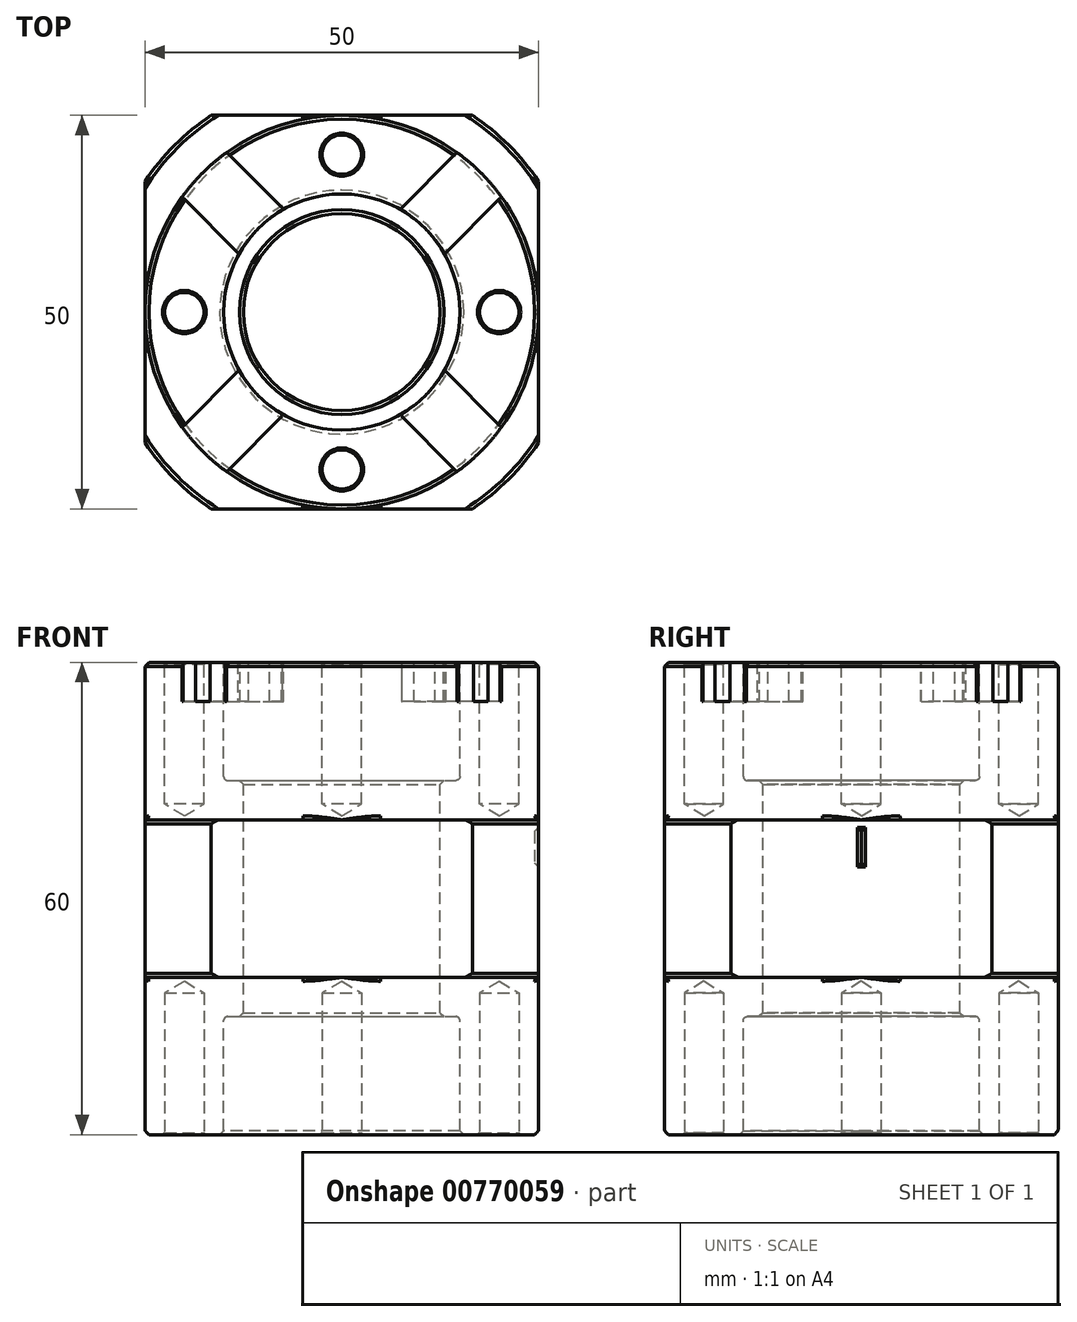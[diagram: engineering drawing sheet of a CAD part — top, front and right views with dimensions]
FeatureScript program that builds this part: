
annotation { "Feature Type Name" : "Feature", "Feature Type Description" : "" }
export const myFeature = defineFeature(function(context is Context, id is Id, definition is map)
    precondition{}
    {
        {
            var Q0;
            Q0=qCreatedBy(makeId("Front.planeOp"),FACE);
            var sketch = newSketch(context, id + "F0", { "sketchPlane" : qUnion([Q0])});
            skLineSegment(sketch, "E0", {"start": v(0, 0) * mm, "end": v(0, -30) * mm, "construction": true});
            skLineSegment(sketch, "E1", {"start": v(15, 0) * mm, "end": v(25, 0) * mm});
            skLineSegment(sketch, "E2", {"start": v(25, -20) * mm, "end": v(30, -20) * mm});
            skLineSegment(sketch, "E3", {"start": v(30, -20) * mm, "end": v(30, -30) * mm});
            skLineSegment(sketch, "E4", {"start": v(15, 0) * mm, "end": v(15, -15) * mm});
            skLineSegment(sketch, "E5", {"start": v(15, -15) * mm, "end": v(12.5, -15) * mm});
            skLineSegment(sketch, "E6", {"start": v(12.5, -15) * mm, "end": v(12.5, -30) * mm});
            skLineSegment(sketch, "E7", {"start": v(25, 0) * mm, "end": v(25, -20) * mm});
            skLineSegment(sketch, "E8", {"start": v(12.5, -30) * mm, "end": v(30, -30) * mm, "construction": true});
            skLineSegment(sketch, "E9.MirrorCS", {"start": v(15, -60) * mm, "end": v(25, -60) * mm});
            skLineSegment(sketch, "E10.MirrorCS", {"start": v(15, -45) * mm, "end": v(12.5, -45) * mm});
            skLineSegment(sketch, "E11.MirrorCS", {"start": v(30, -40) * mm, "end": v(30, -30) * mm});
            skLineSegment(sketch, "E12.MirrorCS", {"start": v(12.5, -45) * mm, "end": v(12.5, -30) * mm});
            skLineSegment(sketch, "E13.MirrorCS", {"start": v(25, -60) * mm, "end": v(25, -40) * mm});
            skLineSegment(sketch, "E14.MirrorCS", {"start": v(15, -60) * mm, "end": v(15, -45) * mm});
            skLineSegment(sketch, "E15.MirrorCS", {"start": v(25, -40) * mm, "end": v(30, -40) * mm});
            skSolve(sketch);
        }
        {
            var Q0;
            Q0 = qSketchRegion(id + "F0", true);
            var Q1;
            Q1=sQuery(id+"F0.wireOp",EDGE,"E0");
            revolve(context, id + "F1", {"surfaceOperationType" : NewSurfaceOperationType.NEW, "entities" : qUnion([Q0]), "axis" : qUnion([Q1]), "revolveType" : RevolveType.FULL});
        }
        {
            var Q0;
            Q0=makeQuery(id+"F1.opRevolve","SWEPT_FACE",FACE,{"disambiguationData":[OSD([sQuery(id+"F0.wireOp",EDGE,"E2")])]});
            var sketch = newSketch(context, id + "F2", { "sketchPlane" : qUnion([Q0])});
            skPoint(sketch, "E16.middle", {"position": v(0, 0) * mm});
            skLineSegment(sketch, "E17.bottom", {"start": v(-30, 30) * mm, "end": v(30, 30) * mm});
            skLineSegment(sketch, "E17.top", {"start": v(-30, -30) * mm, "end": v(30, -30) * mm});
            skLineSegment(sketch, "E17.left", {"start": v(-30, 30) * mm, "end": v(-30, -30) * mm});
            skLineSegment(sketch, "E17.right", {"start": v(30, 30) * mm, "end": v(30, -30) * mm});
            skLineSegment(sketch, "E18.bottom", {"start": v(-25, 25) * mm, "end": v(25, 25) * mm});
            skLineSegment(sketch, "E18.top", {"start": v(-25, -25) * mm, "end": v(25, -25) * mm});
            skLineSegment(sketch, "E18.left", {"start": v(-25, 25) * mm, "end": v(-25, -25) * mm});
            skLineSegment(sketch, "E18.right", {"start": v(25, 25) * mm, "end": v(25, -25) * mm});
            skSolve(sketch);
        }
        {
            var Q0;
            {var subQ0=sQuery(id+"F2.wireOp",EDGE,"E18.bottom");var subQ1=sQuery(id+"F0.wireOp",EDGE,"E2");var subQ2=makeQuery(id+"F1.opRevolve","SWEPT_EDGE",EDGE,{"disambiguationData":[OSD([subQ1,sQuery(id+"F0.wireOp",EDGE,"E3")])]});var subQ3=makeQuery(id+"F2.imprint","INTERSECT",VERTEX,{"disambiguationData":[OD(0.0)],"derivedFrom":[subQ2,subQ0]});Q0=makeQuery(id+"F2.imprint","IMPRINT",FACE,{"disambiguationData":[TD([[makeQuery(id+"F2.imprint","IMPRINT",EDGE,{"disambiguationData":[TD([[subQ3,-1.0]])],"derivedFrom":subQ0}),1.0]])]});}
            var Q1;
            {var subQ0=sQuery(id+"F2.wireOp",EDGE,"E18.right");var subQ1=sQuery(id+"F0.wireOp",EDGE,"E2");var subQ2=makeQuery(id+"F1.opRevolve","SWEPT_EDGE",EDGE,{"disambiguationData":[OSD([subQ1,sQuery(id+"F0.wireOp",EDGE,"E3")])]});var subQ3=makeQuery(id+"F2.imprint","INTERSECT",VERTEX,{"disambiguationData":[OD(0.0)],"derivedFrom":[subQ2,subQ0]});Q1=makeQuery(id+"F2.imprint","IMPRINT",FACE,{"disambiguationData":[TD([[makeQuery(id+"F2.imprint","IMPRINT",EDGE,{"disambiguationData":[TD([[subQ3,-1.0]])],"derivedFrom":subQ0}),1.0]])]});}
            var Q2;
            {var subQ0=sQuery(id+"F2.wireOp",EDGE,"E18.left");var subQ1=sQuery(id+"F0.wireOp",EDGE,"E2");var subQ2=makeQuery(id+"F1.opRevolve","SWEPT_EDGE",EDGE,{"disambiguationData":[OSD([subQ1,sQuery(id+"F0.wireOp",EDGE,"E3")])]});var subQ3=makeQuery(id+"F2.imprint","INTERSECT",VERTEX,{"disambiguationData":[OD(0.0)],"derivedFrom":[subQ2,subQ0]});Q2=makeQuery(id+"F2.imprint","IMPRINT",FACE,{"disambiguationData":[TD([[makeQuery(id+"F2.imprint","IMPRINT",EDGE,{"disambiguationData":[TD([[subQ3,-1.0]])],"derivedFrom":subQ0}),-1.0]])]});}
            var Q3;
            {var subQ0=sQuery(id+"F2.wireOp",EDGE,"E18.top");var subQ1=sQuery(id+"F0.wireOp",EDGE,"E2");var subQ2=makeQuery(id+"F1.opRevolve","SWEPT_EDGE",EDGE,{"disambiguationData":[OSD([subQ1,sQuery(id+"F0.wireOp",EDGE,"E3")])]});var subQ3=makeQuery(id+"F2.imprint","INTERSECT",VERTEX,{"disambiguationData":[OD(0.0)],"derivedFrom":[subQ2,subQ0]});Q3=makeQuery(id+"F2.imprint","IMPRINT",FACE,{"disambiguationData":[TD([[makeQuery(id+"F2.imprint","IMPRINT",EDGE,{"disambiguationData":[TD([[subQ3,-1.0]])],"derivedFrom":subQ0}),-1.0]])]});}
            extrude(context, id + "F3", {"entities" : qUnion([Q0, Q1, Q2, Q3]), "operationType" : NewBodyOperationType.REMOVE, "endBound" : BoundingType.UP_TO_NEXT, "oppositeDirection" : true, "depth" : 26 * mm, "offsetDistance" : 25 * mm});
        }
        {
            var Q0;
            Q0=makeQuery(id+"F1.opRevolve","SWEPT_FACE",FACE,{"disambiguationData":[OSD([sQuery(id+"F0.wireOp",EDGE,"E1")])]});
            var sketch = newSketch(context, id + "F4", { "sketchPlane" : qUnion([Q0])});
            skLineSegment(sketch, "E19", {"start": v(0, 0) * mm, "end": v(31.82, 31.82) * mm, "construction": true});
            skPoint(sketch, "E20.center", {"position": v(0, 0) * mm});
            skLineSegment(sketch, "E21", {"start": v(14.62, 20.28) * mm, "end": v(7.4, 13.05) * mm});
            skArc(sketch, "E22", {"start": v(17.68, 17.68) * mm, "mid": v(16.2, 19.04) * mm, "end": v(14.62, 20.28) * mm});
            skArc(sketch, "E23", {"start": v(10.6, 10.6) * mm, "mid": v(9.08, 11.94) * mm, "end": v(7.4, 13.05) * mm});
            skLineSegment(sketch, "E24.MirrorCS", {"start": v(20.28, 14.62) * mm, "end": v(13.05, 7.4) * mm});
            skArc(sketch, "E25.MirrorCS", {"start": v(17.68, 17.68) * mm, "mid": v(19.04, 16.2) * mm, "end": v(20.28, 14.62) * mm});
            skArc(sketch, "E26.MirrorCS", {"start": v(10.6, 10.6) * mm, "mid": v(11.94, 9.08) * mm, "end": v(13.05, 7.4) * mm});
            skLineSegment(sketch, "E27.1.0", {"start": v(-20.28, 14.62) * mm, "end": v(-13.05, 7.4) * mm});
            skArc(sketch, "E27.1.1", {"start": v(-17.68, 17.68) * mm, "mid": v(-19.04, 16.2) * mm, "end": v(-20.28, 14.62) * mm});
            skArc(sketch, "E27.1.2", {"start": v(-17.68, 17.68) * mm, "mid": v(-16.2, 19.04) * mm, "end": v(-14.62, 20.28) * mm});
            skLineSegment(sketch, "E27.1.3", {"start": v(-14.62, 20.28) * mm, "end": v(-7.4, 13.05) * mm});
            skArc(sketch, "E27.1.4", {"start": v(-10.6, 10.6) * mm, "mid": v(-9.08, 11.94) * mm, "end": v(-7.4, 13.05) * mm});
            skArc(sketch, "E27.1.5", {"start": v(-10.6, 10.6) * mm, "mid": v(-11.94, 9.08) * mm, "end": v(-13.05, 7.4) * mm});
            skLineSegment(sketch, "E27.1.6", {"start": v(0, 0) * mm, "end": v(-31.82, 31.82) * mm, "construction": true});
            skLineSegment(sketch, "E27.2.0", {"start": v(-14.62, -20.28) * mm, "end": v(-7.4, -13.05) * mm});
            skArc(sketch, "E27.2.1", {"start": v(-17.68, -17.68) * mm, "mid": v(-16.2, -19.04) * mm, "end": v(-14.62, -20.28) * mm});
            skArc(sketch, "E27.2.2", {"start": v(-17.68, -17.68) * mm, "mid": v(-19.04, -16.2) * mm, "end": v(-20.28, -14.62) * mm});
            skLineSegment(sketch, "E27.2.3", {"start": v(-20.28, -14.62) * mm, "end": v(-13.05, -7.4) * mm});
            skArc(sketch, "E27.2.4", {"start": v(-10.6, -10.6) * mm, "mid": v(-11.94, -9.08) * mm, "end": v(-13.05, -7.4) * mm});
            skArc(sketch, "E27.2.5", {"start": v(-10.6, -10.6) * mm, "mid": v(-9.08, -11.94) * mm, "end": v(-7.4, -13.05) * mm});
            skLineSegment(sketch, "E27.2.6", {"start": v(0, 0) * mm, "end": v(-31.82, -31.82) * mm, "construction": true});
            skLineSegment(sketch, "E27.3.0", {"start": v(20.28, -14.62) * mm, "end": v(13.05, -7.4) * mm});
            skArc(sketch, "E27.3.1", {"start": v(17.68, -17.68) * mm, "mid": v(19.04, -16.2) * mm, "end": v(20.28, -14.62) * mm});
            skArc(sketch, "E27.3.2", {"start": v(17.68, -17.68) * mm, "mid": v(16.2, -19.04) * mm, "end": v(14.62, -20.28) * mm});
            skLineSegment(sketch, "E27.3.3", {"start": v(14.62, -20.28) * mm, "end": v(7.4, -13.05) * mm});
            skArc(sketch, "E27.3.4", {"start": v(10.6, -10.6) * mm, "mid": v(9.08, -11.94) * mm, "end": v(7.4, -13.05) * mm});
            skArc(sketch, "E27.3.5", {"start": v(10.6, -10.6) * mm, "mid": v(11.94, -9.08) * mm, "end": v(13.05, -7.4) * mm});
            skLineSegment(sketch, "E27.3.6", {"start": v(0, 0) * mm, "end": v(31.82, -31.82) * mm, "construction": true});
            skSolve(sketch);
        }
        {
            var Q0;
            Q0 = qSketchRegion(id + "F4", true);
            extrude(context, id + "F5", {"entities" : qUnion([Q0]), "operationType" : NewBodyOperationType.REMOVE, "oppositeDirection" : true, "depth" : 5 * mm, "offsetDistance" : 25 * mm});
        }
        {
            var Q0;
            Q0=makeQuery(id+"F5.boolean.opBoolean","SPLIT",FACE,{"disambiguationData":[TD([makeQuery(id+"F5.opExtrude","SWEPT_FACE",FACE,{"disambiguationData":[OSD([sQuery(id+"F4.wireOp",EDGE,"E21")])]})])],"derivedFrom":makeQuery(id+"F1.opRevolve","SWEPT_FACE",FACE,{"disambiguationData":[OSD([sQuery(id+"F0.wireOp",EDGE,"E1")])]})});
            var sketch = newSketch(context, id + "F6", { "sketchPlane" : qUnion([Q0])});
            skLineSegment(sketch, "E28", {"start": v(0, 0) * mm, "end": v(20, 0) * mm, "construction": true});
            skCircle(sketch, "E29", {"center": v(0, 0) * mm, "radius": 20 * mm, "construction": true});
            skLineSegment(sketch, "E30.1.0", {"start": v(0, 0) * mm, "end": v(0, 20) * mm, "construction": true});
            skLineSegment(sketch, "E30.2.0", {"start": v(0, 0) * mm, "end": v(-20, 0) * mm, "construction": true});
            skLineSegment(sketch, "E30.3.0", {"start": v(0, 0) * mm, "end": v(0, -20) * mm, "construction": true});
            skSolve(sketch);
        }
        {
            var Q0;
            Q0=sQuery(id+"F6.wireOp",VERTEX,"E30.1.0.end");
            var Q1;
            Q1=sQuery(id+"F6.wireOp",VERTEX,"E28.end");
            var Q2;
            Q2=sQuery(id+"F6.wireOp",VERTEX,"E30.3.0.end");
            var Q3;
            Q3=sQuery(id+"F6.wireOp",VERTEX,"E30.2.0.end");
            var Q4;
            Q4=makeQuery(id+"F1.opRevolve","SWEPT_BODY",BODY,{"disambiguationData":[OSD([sQuery(id+"F0.wireOp",EDGE,"E1"),sQuery(id+"F0.wireOp",EDGE,"E2"),sQuery(id+"F0.wireOp",EDGE,"E3"),sQuery(id+"F0.wireOp",EDGE,"E4"),sQuery(id+"F0.wireOp",EDGE,"E5"),sQuery(id+"F0.wireOp",EDGE,"E6"),sQuery(id+"F0.wireOp",EDGE,"E7"),sQuery(id+"F0.wireOp",EDGE,"E9.MirrorCS"),sQuery(id+"F0.wireOp",EDGE,"E10.MirrorCS"),sQuery(id+"F0.wireOp",EDGE,"E11.MirrorCS"),sQuery(id+"F0.wireOp",EDGE,"E12.MirrorCS"),sQuery(id+"F0.wireOp",EDGE,"E13.MirrorCS"),sQuery(id+"F0.wireOp",EDGE,"E14.MirrorCS"),sQuery(id+"F0.wireOp",EDGE,"E15.MirrorCS")])]});
            hole(context, id + "F7", {"style" : HoleStyle.C_SINK, "endStyle" : HoleEndStyle.BLIND, "holeDiameter" : 5 * mm, "cSinkDiameter" : 5.5 * mm, "cSinkAngle" : 90 * degree, "majorDiameter" : 5 * mm, "holeDepth" : 18 * mm, "isTappedThrough" : true, "tappedDepth" : 5 * mm, "tapClearance" : 3, "startFromSketch" : true, "locations" : qUnion([Q0, Q1, Q2, Q3]), "scope" : qUnion([Q4])});
        }
        {
            var Q0;
            Q0=makeQuery(id+"F3.boolean.opBoolean","COPY",FACE,{"derivedFrom":makeQuery(id+"F3.opExtrude","SWEPT_FACE",FACE,{"disambiguationData":[OSD([sQuery(id+"F2.wireOp",EDGE,"E18.right")])]})});
            var sketch = newSketch(context, id + "F8", { "sketchPlane" : qUnion([Q0])});
            skLineSegment(sketch, "E31.bottom", {"start": v(0.5, -26) * mm, "end": v(-0.5, -26) * mm});
            skLineSegment(sketch, "E31.left", {"start": v(0.5, -26) * mm, "end": v(0.5, -21) * mm});
            skLineSegment(sketch, "E31.right", {"start": v(-0.5, -26) * mm, "end": v(-0.5, -21) * mm});
            skPoint(sketch, "E31.middle", {"position": v(0, -20) * mm});
            skLineSegment(sketch, "E32", {"start": v(0.5, -21) * mm, "end": v(-0.5, -21) * mm});
            skSolve(sketch);
        }
        {
            var Q0;
            Q0=makeQuery(id+"F8.imprint","IMPRINT",FACE,{"disambiguationData":[TD([[makeQuery(id+"F8.imprint","IMPRINT",EDGE,{"derivedFrom":sQuery(id+"F8.wireOp",EDGE,"E31.bottom")}),-1.0]])]});
            extrude(context, id + "F9", {"entities" : qUnion([Q0]), "operationType" : NewBodyOperationType.REMOVE, "oppositeDirection" : true, "depth" : 0.5 * mm, "offsetDistance" : 25 * mm, "hasDraft" : true, "draftAngle" : 45 * degree, "draftPullDirection" : true});
        }
        {
            var Q0;
            Q0=makeQuery(id+"F1.opRevolve","SWEPT_FACE",FACE,{"disambiguationData":[OSD([sQuery(id+"F0.wireOp",EDGE,"E9.MirrorCS")])]});
            var sketch = newSketch(context, id + "F10", { "sketchPlane" : qUnion([Q0])});
            skLineSegment(sketch, "E33", {"start": v(0, 0) * mm, "end": v(20, 0) * mm, "construction": true});
            skCircle(sketch, "E34", {"center": v(0, 0) * mm, "radius": 20 * mm, "construction": true});
            skLineSegment(sketch, "E35.1.0", {"start": v(0, 0) * mm, "end": v(0, 20) * mm, "construction": true});
            skLineSegment(sketch, "E35.2.0", {"start": v(0, 0) * mm, "end": v(-20, 0) * mm, "construction": true});
            skLineSegment(sketch, "E35.3.0", {"start": v(0, 0) * mm, "end": v(0, -20) * mm, "construction": true});
            skSolve(sketch);
        }
        {
            var Q0;
            Q0=sQuery(id+"F10.wireOp",VERTEX,"E33.end");
            var Q1;
            Q1=sQuery(id+"F10.wireOp",VERTEX,"E35.1.0.end");
            var Q2;
            Q2=sQuery(id+"F10.wireOp",VERTEX,"E35.2.0.end");
            var Q3;
            Q3=sQuery(id+"F10.wireOp",VERTEX,"E35.3.0.end");
            var Q4;
            Q4=makeQuery(id+"F1.opRevolve","SWEPT_BODY",BODY,{"disambiguationData":[OSD([sQuery(id+"F0.wireOp",EDGE,"E1"),sQuery(id+"F0.wireOp",EDGE,"E2"),sQuery(id+"F0.wireOp",EDGE,"E3"),sQuery(id+"F0.wireOp",EDGE,"E4"),sQuery(id+"F0.wireOp",EDGE,"E5"),sQuery(id+"F0.wireOp",EDGE,"E6"),sQuery(id+"F0.wireOp",EDGE,"E7"),sQuery(id+"F0.wireOp",EDGE,"E9.MirrorCS"),sQuery(id+"F0.wireOp",EDGE,"E10.MirrorCS"),sQuery(id+"F0.wireOp",EDGE,"E11.MirrorCS"),sQuery(id+"F0.wireOp",EDGE,"E12.MirrorCS"),sQuery(id+"F0.wireOp",EDGE,"E13.MirrorCS"),sQuery(id+"F0.wireOp",EDGE,"E14.MirrorCS"),sQuery(id+"F0.wireOp",EDGE,"E15.MirrorCS")])]});
            hole(context, id + "F11", {"style" : HoleStyle.C_SINK, "endStyle" : HoleEndStyle.BLIND, "holeDiameter" : 5 * mm, "cSinkDiameter" : 5.5 * mm, "cSinkAngle" : 90 * degree, "majorDiameter" : 5 * mm, "holeDepth" : 18 * mm, "isTappedThrough" : true, "tappedDepth" : 5 * mm, "tapClearance" : 3, "startFromSketch" : true, "locations" : qUnion([Q0, Q1, Q2, Q3]), "scope" : qUnion([Q4])});
        }
        {
            var Q0;
            Q0=makeQuery(id+"F1.opRevolve","SWEPT_FACE",FACE,{"disambiguationData":[OSD([sQuery(id+"F0.wireOp",EDGE,"E9.MirrorCS")])]});
            var sketch = newSketch(context, id + "F12", { "sketchPlane" : qUnion([Q0])});
            skLineSegment(sketch, "E36", {"start": v(0, 0) * mm, "end": v(31.82, 31.82) * mm, "construction": true});
            skPoint(sketch, "E37.center", {"position": v(0, 0) * mm});
            skLineSegment(sketch, "E38", {"start": v(14.62, 20.28) * mm, "end": v(7.4, 13.05) * mm});
            skArc(sketch, "E39", {"start": v(17.68, 17.68) * mm, "mid": v(16.2, 19.04) * mm, "end": v(14.62, 20.28) * mm});
            skArc(sketch, "E40", {"start": v(10.6, 10.6) * mm, "mid": v(9.08, 11.94) * mm, "end": v(7.4, 13.05) * mm});
            skLineSegment(sketch, "E41.MirrorCS", {"start": v(20.28, 14.62) * mm, "end": v(13.05, 7.4) * mm});
            skArc(sketch, "E42.MirrorCS", {"start": v(17.68, 17.68) * mm, "mid": v(19.04, 16.2) * mm, "end": v(20.28, 14.62) * mm});
            skArc(sketch, "E43.MirrorCS", {"start": v(10.6, 10.6) * mm, "mid": v(11.94, 9.08) * mm, "end": v(13.05, 7.4) * mm});
            skLineSegment(sketch, "E44.1.0", {"start": v(-20.28, 14.62) * mm, "end": v(-13.05, 7.4) * mm});
            skArc(sketch, "E44.1.1", {"start": v(-17.68, 17.68) * mm, "mid": v(-19.04, 16.2) * mm, "end": v(-20.28, 14.62) * mm});
            skArc(sketch, "E44.1.2", {"start": v(-17.68, 17.68) * mm, "mid": v(-16.2, 19.04) * mm, "end": v(-14.62, 20.28) * mm});
            skLineSegment(sketch, "E44.1.3", {"start": v(-14.62, 20.28) * mm, "end": v(-7.4, 13.05) * mm});
            skArc(sketch, "E44.1.4", {"start": v(-10.6, 10.6) * mm, "mid": v(-9.08, 11.94) * mm, "end": v(-7.4, 13.05) * mm});
            skArc(sketch, "E44.1.5", {"start": v(-10.6, 10.6) * mm, "mid": v(-11.94, 9.08) * mm, "end": v(-13.05, 7.4) * mm});
            skLineSegment(sketch, "E44.1.6", {"start": v(0, 0) * mm, "end": v(-31.82, 31.82) * mm, "construction": true});
            skLineSegment(sketch, "E44.2.0", {"start": v(-14.62, -20.28) * mm, "end": v(-7.4, -13.05) * mm});
            skArc(sketch, "E44.2.1", {"start": v(-17.68, -17.68) * mm, "mid": v(-16.2, -19.04) * mm, "end": v(-14.62, -20.28) * mm});
            skArc(sketch, "E44.2.2", {"start": v(-17.68, -17.68) * mm, "mid": v(-19.04, -16.2) * mm, "end": v(-20.28, -14.62) * mm});
            skLineSegment(sketch, "E44.2.3", {"start": v(-20.28, -14.62) * mm, "end": v(-13.05, -7.4) * mm});
            skArc(sketch, "E44.2.4", {"start": v(-10.6, -10.6) * mm, "mid": v(-11.94, -9.08) * mm, "end": v(-13.05, -7.4) * mm});
            skArc(sketch, "E44.2.5", {"start": v(-10.6, -10.6) * mm, "mid": v(-9.08, -11.94) * mm, "end": v(-7.4, -13.05) * mm});
            skLineSegment(sketch, "E44.2.6", {"start": v(0, 0) * mm, "end": v(-31.82, -31.82) * mm, "construction": true});
            skLineSegment(sketch, "E44.3.0", {"start": v(20.28, -14.62) * mm, "end": v(13.05, -7.4) * mm});
            skArc(sketch, "E44.3.1", {"start": v(17.68, -17.68) * mm, "mid": v(19.04, -16.2) * mm, "end": v(20.28, -14.62) * mm});
            skArc(sketch, "E44.3.2", {"start": v(17.68, -17.68) * mm, "mid": v(16.2, -19.04) * mm, "end": v(14.62, -20.28) * mm});
            skLineSegment(sketch, "E44.3.3", {"start": v(14.62, -20.28) * mm, "end": v(7.4, -13.05) * mm});
            skArc(sketch, "E44.3.4", {"start": v(10.6, -10.6) * mm, "mid": v(9.08, -11.94) * mm, "end": v(7.4, -13.05) * mm});
            skArc(sketch, "E44.3.5", {"start": v(10.6, -10.6) * mm, "mid": v(11.94, -9.08) * mm, "end": v(13.05, -7.4) * mm});
            skLineSegment(sketch, "E44.3.6", {"start": v(0, 0) * mm, "end": v(31.82, -31.82) * mm, "construction": true});
            skSolve(sketch);
        }
        {
            var Q0;
            Q0=makeQuery(id+"F12.imprint","IMPRINT",FACE,{"disambiguationData":[TD([[makeQuery(id+"F12.imprint","IMPRINT",EDGE,{"derivedFrom":sQuery(id+"F12.wireOp",EDGE,"E44.1.0")}),1.0]])]});
            var Q1;
            Q1=makeQuery(id+"F12.imprint","IMPRINT",FACE,{"disambiguationData":[TD([[makeQuery(id+"F12.imprint","IMPRINT",EDGE,{"derivedFrom":sQuery(id+"F12.wireOp",EDGE,"E38")}),1.0]])]});
            var Q2;
            Q2=makeQuery(id+"F12.imprint","IMPRINT",FACE,{"disambiguationData":[TD([[makeQuery(id+"F12.imprint","IMPRINT",EDGE,{"derivedFrom":sQuery(id+"F12.wireOp",EDGE,"E44.3.0")}),1.0]])]});
            var Q3;
            Q3=makeQuery(id+"F12.imprint","IMPRINT",FACE,{"disambiguationData":[TD([[makeQuery(id+"F12.imprint","IMPRINT",EDGE,{"derivedFrom":sQuery(id+"F12.wireOp",EDGE,"E44.2.0")}),1.0]])]});
            extrude(context, id + "F13", {"entities" : qUnion([Q0, Q1, Q2, Q3]), "operationType" : NewBodyOperationType.REMOVE, "oppositeDirection" : true, "depth" : 5 * mm, "offsetDistance" : 25 * mm});
        }
        {
            var Q0;
            {var subQ0=sQuery(id+"F0.wireOp",EDGE,"E1");var subQ1=sQuery(id+"F0.wireOp",EDGE,"E7");Q0=makeQuery(id+"F5.boolean.opBoolean","SPLIT",EDGE,{"disambiguationData":[TD([makeQuery(id+"F5.opExtrude","SWEPT_FACE",FACE,{"disambiguationData":[OSD([sQuery(id+"F4.wireOp",EDGE,"E27.1.0")])]})])],"derivedFrom":makeQuery(id+"F1.opRevolve","SWEPT_EDGE",EDGE,{"disambiguationData":[OSD([subQ0,subQ1])]})});}
            var Q1;
            {var subQ0=sQuery(id+"F0.wireOp",EDGE,"E1");var subQ1=sQuery(id+"F0.wireOp",EDGE,"E7");Q1=makeQuery(id+"F5.boolean.opBoolean","SPLIT",EDGE,{"disambiguationData":[TD([makeQuery(id+"F5.opExtrude","SWEPT_FACE",FACE,{"disambiguationData":[OSD([sQuery(id+"F4.wireOp",EDGE,"E21")])]})])],"derivedFrom":makeQuery(id+"F1.opRevolve","SWEPT_EDGE",EDGE,{"disambiguationData":[OSD([subQ0,subQ1])]})});}
            var Q2;
            {var subQ0=sQuery(id+"F0.wireOp",EDGE,"E1");var subQ1=sQuery(id+"F0.wireOp",EDGE,"E7");Q2=makeQuery(id+"F5.boolean.opBoolean","SPLIT",EDGE,{"disambiguationData":[TD([makeQuery(id+"F5.opExtrude","SWEPT_FACE",FACE,{"disambiguationData":[OSD([sQuery(id+"F4.wireOp",EDGE,"E24.MirrorCS")])]})])],"derivedFrom":makeQuery(id+"F1.opRevolve","SWEPT_EDGE",EDGE,{"disambiguationData":[OSD([subQ0,subQ1])]})});}
            var Q3;
            {var subQ0=sQuery(id+"F0.wireOp",EDGE,"E1");var subQ1=sQuery(id+"F0.wireOp",EDGE,"E7");Q3=makeQuery(id+"F5.boolean.opBoolean","SPLIT",EDGE,{"disambiguationData":[TD([makeQuery(id+"F5.opExtrude","SWEPT_FACE",FACE,{"disambiguationData":[OSD([sQuery(id+"F4.wireOp",EDGE,"E27.2.0")])]})])],"derivedFrom":makeQuery(id+"F1.opRevolve","SWEPT_EDGE",EDGE,{"disambiguationData":[OSD([subQ0,subQ1])]})});}
            var Q4;
            {var subQ0=sQuery(id+"F0.wireOp",EDGE,"E1");var subQ1=sQuery(id+"F0.wireOp",EDGE,"E4");Q4=makeQuery(id+"F5.boolean.opBoolean","SPLIT",EDGE,{"disambiguationData":[TD([makeQuery(id+"F5.opExtrude","SWEPT_FACE",FACE,{"disambiguationData":[OSD([sQuery(id+"F4.wireOp",EDGE,"E21")])]})])],"derivedFrom":makeQuery(id+"F1.opRevolve","SWEPT_EDGE",EDGE,{"disambiguationData":[OSD([subQ0,subQ1])]})});}
            var Q5;
            {var subQ0=sQuery(id+"F0.wireOp",EDGE,"E1");var subQ1=sQuery(id+"F0.wireOp",EDGE,"E4");Q5=makeQuery(id+"F5.boolean.opBoolean","SPLIT",EDGE,{"disambiguationData":[TD([makeQuery(id+"F5.opExtrude","SWEPT_FACE",FACE,{"disambiguationData":[OSD([sQuery(id+"F4.wireOp",EDGE,"E24.MirrorCS")])]})])],"derivedFrom":makeQuery(id+"F1.opRevolve","SWEPT_EDGE",EDGE,{"disambiguationData":[OSD([subQ0,subQ1])]})});}
            var Q6;
            {var subQ0=sQuery(id+"F0.wireOp",EDGE,"E1");var subQ1=sQuery(id+"F0.wireOp",EDGE,"E4");Q6=makeQuery(id+"F5.boolean.opBoolean","SPLIT",EDGE,{"disambiguationData":[TD([makeQuery(id+"F5.opExtrude","SWEPT_FACE",FACE,{"disambiguationData":[OSD([sQuery(id+"F4.wireOp",EDGE,"E27.1.0")])]})])],"derivedFrom":makeQuery(id+"F1.opRevolve","SWEPT_EDGE",EDGE,{"disambiguationData":[OSD([subQ0,subQ1])]})});}
            var Q7;
            {var subQ0=sQuery(id+"F0.wireOp",EDGE,"E1");var subQ1=sQuery(id+"F0.wireOp",EDGE,"E4");Q7=makeQuery(id+"F5.boolean.opBoolean","SPLIT",EDGE,{"disambiguationData":[TD([makeQuery(id+"F5.opExtrude","SWEPT_FACE",FACE,{"disambiguationData":[OSD([sQuery(id+"F4.wireOp",EDGE,"E27.2.0")])]})])],"derivedFrom":makeQuery(id+"F1.opRevolve","SWEPT_EDGE",EDGE,{"disambiguationData":[OSD([subQ0,subQ1])]})});}
            var Q8;
            Q8=makeQuery(id+"F1.opRevolve","SWEPT_EDGE",EDGE,{"disambiguationData":[OSD([sQuery(id+"F0.wireOp",EDGE,"E5"),sQuery(id+"F0.wireOp",EDGE,"E6")])]});
            var Q9;
            {var subQ0=sQuery(id+"F0.wireOp",EDGE,"E2");var subQ1=sQuery(id+"F0.wireOp",EDGE,"E3");Q9=makeQuery(id+"F3.boolean.opBoolean","SPLIT",EDGE,{"disambiguationData":[TD([makeQuery(id+"F1.opRevolve","SWEPT_FACE",FACE,{"disambiguationData":[OSD([subQ0])]}),makeQuery(id+"F1.opRevolve","SWEPT_FACE",FACE,{"disambiguationData":[OSD([subQ1,sQuery(id+"F0.wireOp",EDGE,"E11.MirrorCS")])]}),makeQuery(id+"F3.opExtrude","SWEPT_FACE",FACE,{"disambiguationData":[OSD([sQuery(id+"F2.wireOp",EDGE,"E18.bottom")])]}),makeQuery(id+"F3.opExtrude","SWEPT_FACE",FACE,{"disambiguationData":[OSD([sQuery(id+"F2.wireOp",EDGE,"E18.right")])]})])],"derivedFrom":makeQuery(id+"F1.opRevolve","SWEPT_EDGE",EDGE,{"disambiguationData":[OSD([subQ0,subQ1])]})});}
            var Q10;
            {var subQ0=sQuery(id+"F0.wireOp",EDGE,"E11.MirrorCS");var subQ1=sQuery(id+"F0.wireOp",EDGE,"E15.MirrorCS");Q10=makeQuery(id+"F3.boolean.opBoolean","SPLIT",EDGE,{"disambiguationData":[TD([makeQuery(id+"F1.opRevolve","SWEPT_FACE",FACE,{"disambiguationData":[OSD([sQuery(id+"F0.wireOp",EDGE,"E3"),subQ0])]}),makeQuery(id+"F1.opRevolve","SWEPT_FACE",FACE,{"disambiguationData":[OSD([subQ1])]}),makeQuery(id+"F3.opExtrude","SWEPT_FACE",FACE,{"disambiguationData":[OSD([sQuery(id+"F2.wireOp",EDGE,"E18.bottom")])]}),makeQuery(id+"F3.opExtrude","SWEPT_FACE",FACE,{"disambiguationData":[OSD([sQuery(id+"F2.wireOp",EDGE,"E18.right")])]})])],"derivedFrom":makeQuery(id+"F1.opRevolve","SWEPT_EDGE",EDGE,{"disambiguationData":[OSD([subQ0,subQ1])]})});}
            var Q11;
            {var subQ0=sQuery(id+"F0.wireOp",EDGE,"E2");var subQ1=sQuery(id+"F0.wireOp",EDGE,"E3");Q11=makeQuery(id+"F3.boolean.opBoolean","SPLIT",EDGE,{"disambiguationData":[TD([makeQuery(id+"F1.opRevolve","SWEPT_FACE",FACE,{"disambiguationData":[OSD([subQ0])]}),makeQuery(id+"F1.opRevolve","SWEPT_FACE",FACE,{"disambiguationData":[OSD([subQ1,sQuery(id+"F0.wireOp",EDGE,"E11.MirrorCS")])]}),makeQuery(id+"F3.opExtrude","SWEPT_FACE",FACE,{"disambiguationData":[OSD([sQuery(id+"F2.wireOp",EDGE,"E18.bottom")])]}),makeQuery(id+"F3.opExtrude","SWEPT_FACE",FACE,{"disambiguationData":[OSD([sQuery(id+"F2.wireOp",EDGE,"E18.left")])]})])],"derivedFrom":makeQuery(id+"F1.opRevolve","SWEPT_EDGE",EDGE,{"disambiguationData":[OSD([subQ0,subQ1])]})});}
            var Q12;
            {var subQ0=sQuery(id+"F0.wireOp",EDGE,"E11.MirrorCS");var subQ1=sQuery(id+"F0.wireOp",EDGE,"E15.MirrorCS");Q12=makeQuery(id+"F3.boolean.opBoolean","SPLIT",EDGE,{"disambiguationData":[TD([makeQuery(id+"F1.opRevolve","SWEPT_FACE",FACE,{"disambiguationData":[OSD([sQuery(id+"F0.wireOp",EDGE,"E3"),subQ0])]}),makeQuery(id+"F1.opRevolve","SWEPT_FACE",FACE,{"disambiguationData":[OSD([subQ1])]}),makeQuery(id+"F3.opExtrude","SWEPT_FACE",FACE,{"disambiguationData":[OSD([sQuery(id+"F2.wireOp",EDGE,"E18.bottom")])]}),makeQuery(id+"F3.opExtrude","SWEPT_FACE",FACE,{"disambiguationData":[OSD([sQuery(id+"F2.wireOp",EDGE,"E18.left")])]})])],"derivedFrom":makeQuery(id+"F1.opRevolve","SWEPT_EDGE",EDGE,{"disambiguationData":[OSD([subQ0,subQ1])]})});}
            var Q13;
            {var subQ0=sQuery(id+"F0.wireOp",EDGE,"E2");var subQ1=sQuery(id+"F0.wireOp",EDGE,"E3");Q13=makeQuery(id+"F3.boolean.opBoolean","SPLIT",EDGE,{"disambiguationData":[TD([makeQuery(id+"F1.opRevolve","SWEPT_FACE",FACE,{"disambiguationData":[OSD([subQ0])]}),makeQuery(id+"F1.opRevolve","SWEPT_FACE",FACE,{"disambiguationData":[OSD([subQ1,sQuery(id+"F0.wireOp",EDGE,"E11.MirrorCS")])]}),makeQuery(id+"F3.opExtrude","SWEPT_FACE",FACE,{"disambiguationData":[OSD([sQuery(id+"F2.wireOp",EDGE,"E18.top")])]}),makeQuery(id+"F3.opExtrude","SWEPT_FACE",FACE,{"disambiguationData":[OSD([sQuery(id+"F2.wireOp",EDGE,"E18.left")])]})])],"derivedFrom":makeQuery(id+"F1.opRevolve","SWEPT_EDGE",EDGE,{"disambiguationData":[OSD([subQ0,subQ1])]})});}
            var Q14;
            {var subQ0=sQuery(id+"F0.wireOp",EDGE,"E11.MirrorCS");var subQ1=sQuery(id+"F0.wireOp",EDGE,"E15.MirrorCS");Q14=makeQuery(id+"F3.boolean.opBoolean","SPLIT",EDGE,{"disambiguationData":[TD([makeQuery(id+"F1.opRevolve","SWEPT_FACE",FACE,{"disambiguationData":[OSD([sQuery(id+"F0.wireOp",EDGE,"E3"),subQ0])]}),makeQuery(id+"F1.opRevolve","SWEPT_FACE",FACE,{"disambiguationData":[OSD([subQ1])]}),makeQuery(id+"F3.opExtrude","SWEPT_FACE",FACE,{"disambiguationData":[OSD([sQuery(id+"F2.wireOp",EDGE,"E18.top")])]}),makeQuery(id+"F3.opExtrude","SWEPT_FACE",FACE,{"disambiguationData":[OSD([sQuery(id+"F2.wireOp",EDGE,"E18.left")])]})])],"derivedFrom":makeQuery(id+"F1.opRevolve","SWEPT_EDGE",EDGE,{"disambiguationData":[OSD([subQ0,subQ1])]})});}
            var Q15;
            {var subQ0=sQuery(id+"F0.wireOp",EDGE,"E2");var subQ1=sQuery(id+"F0.wireOp",EDGE,"E3");Q15=makeQuery(id+"F3.boolean.opBoolean","SPLIT",EDGE,{"disambiguationData":[TD([makeQuery(id+"F1.opRevolve","SWEPT_FACE",FACE,{"disambiguationData":[OSD([subQ0])]}),makeQuery(id+"F1.opRevolve","SWEPT_FACE",FACE,{"disambiguationData":[OSD([subQ1,sQuery(id+"F0.wireOp",EDGE,"E11.MirrorCS")])]}),makeQuery(id+"F3.opExtrude","SWEPT_FACE",FACE,{"disambiguationData":[OSD([sQuery(id+"F2.wireOp",EDGE,"E18.top")])]}),makeQuery(id+"F3.opExtrude","SWEPT_FACE",FACE,{"disambiguationData":[OSD([sQuery(id+"F2.wireOp",EDGE,"E18.right")])]})])],"derivedFrom":makeQuery(id+"F1.opRevolve","SWEPT_EDGE",EDGE,{"disambiguationData":[OSD([subQ0,subQ1])]})});}
            var Q16;
            {var subQ0=sQuery(id+"F0.wireOp",EDGE,"E9.MirrorCS");var subQ1=sQuery(id+"F0.wireOp",EDGE,"E13.MirrorCS");Q16=makeQuery(id+"F13.boolean.opBoolean","SPLIT",EDGE,{"disambiguationData":[TD([makeQuery(id+"F13.opExtrude","SWEPT_FACE",FACE,{"disambiguationData":[OSD([sQuery(id+"F12.wireOp",EDGE,"E44.1.0")])]})])],"derivedFrom":makeQuery(id+"F1.opRevolve","SWEPT_EDGE",EDGE,{"disambiguationData":[OSD([subQ0,subQ1])]})});}
            var Q17;
            {var subQ0=sQuery(id+"F0.wireOp",EDGE,"E9.MirrorCS");var subQ1=sQuery(id+"F0.wireOp",EDGE,"E14.MirrorCS");Q17=makeQuery(id+"F13.boolean.opBoolean","SPLIT",EDGE,{"disambiguationData":[TD([makeQuery(id+"F13.opExtrude","SWEPT_FACE",FACE,{"disambiguationData":[OSD([sQuery(id+"F12.wireOp",EDGE,"E44.1.0")])]})])],"derivedFrom":makeQuery(id+"F1.opRevolve","SWEPT_EDGE",EDGE,{"disambiguationData":[OSD([subQ0,subQ1])]})});}
            var Q18;
            {var subQ0=sQuery(id+"F0.wireOp",EDGE,"E9.MirrorCS");var subQ1=sQuery(id+"F0.wireOp",EDGE,"E14.MirrorCS");Q18=makeQuery(id+"F13.boolean.opBoolean","SPLIT",EDGE,{"disambiguationData":[TD([makeQuery(id+"F13.opExtrude","SWEPT_FACE",FACE,{"disambiguationData":[OSD([sQuery(id+"F12.wireOp",EDGE,"E44.2.0")])]})])],"derivedFrom":makeQuery(id+"F1.opRevolve","SWEPT_EDGE",EDGE,{"disambiguationData":[OSD([subQ0,subQ1])]})});}
            var Q19;
            {var subQ0=sQuery(id+"F0.wireOp",EDGE,"E9.MirrorCS");var subQ1=sQuery(id+"F0.wireOp",EDGE,"E14.MirrorCS");Q19=makeQuery(id+"F13.boolean.opBoolean","SPLIT",EDGE,{"disambiguationData":[TD([makeQuery(id+"F13.opExtrude","SWEPT_FACE",FACE,{"disambiguationData":[OSD([sQuery(id+"F12.wireOp",EDGE,"E41.MirrorCS")])]})])],"derivedFrom":makeQuery(id+"F1.opRevolve","SWEPT_EDGE",EDGE,{"disambiguationData":[OSD([subQ0,subQ1])]})});}
            var Q20;
            {var subQ0=sQuery(id+"F0.wireOp",EDGE,"E9.MirrorCS");var subQ1=sQuery(id+"F0.wireOp",EDGE,"E14.MirrorCS");Q20=makeQuery(id+"F13.boolean.opBoolean","SPLIT",EDGE,{"disambiguationData":[TD([makeQuery(id+"F13.opExtrude","SWEPT_FACE",FACE,{"disambiguationData":[OSD([sQuery(id+"F12.wireOp",EDGE,"E38")])]})])],"derivedFrom":makeQuery(id+"F1.opRevolve","SWEPT_EDGE",EDGE,{"disambiguationData":[OSD([subQ0,subQ1])]})});}
            var Q21;
            {var subQ0=sQuery(id+"F0.wireOp",EDGE,"E9.MirrorCS");var subQ1=sQuery(id+"F0.wireOp",EDGE,"E13.MirrorCS");Q21=makeQuery(id+"F13.boolean.opBoolean","SPLIT",EDGE,{"disambiguationData":[TD([makeQuery(id+"F13.opExtrude","SWEPT_FACE",FACE,{"disambiguationData":[OSD([sQuery(id+"F12.wireOp",EDGE,"E38")])]})])],"derivedFrom":makeQuery(id+"F1.opRevolve","SWEPT_EDGE",EDGE,{"disambiguationData":[OSD([subQ0,subQ1])]})});}
            var Q22;
            Q22=makeQuery(id+"F1.opRevolve","SWEPT_EDGE",EDGE,{"disambiguationData":[OSD([sQuery(id+"F0.wireOp",EDGE,"E10.MirrorCS"),sQuery(id+"F0.wireOp",EDGE,"E12.MirrorCS")])]});
            var Q23;
            {var subQ0=sQuery(id+"F0.wireOp",EDGE,"E9.MirrorCS");var subQ1=sQuery(id+"F0.wireOp",EDGE,"E13.MirrorCS");Q23=makeQuery(id+"F13.boolean.opBoolean","SPLIT",EDGE,{"disambiguationData":[TD([makeQuery(id+"F13.opExtrude","SWEPT_FACE",FACE,{"disambiguationData":[OSD([sQuery(id+"F12.wireOp",EDGE,"E44.2.0")])]})])],"derivedFrom":makeQuery(id+"F1.opRevolve","SWEPT_EDGE",EDGE,{"disambiguationData":[OSD([subQ0,subQ1])]})});}
            var Q24;
            {var subQ0=sQuery(id+"F0.wireOp",EDGE,"E9.MirrorCS");var subQ1=sQuery(id+"F0.wireOp",EDGE,"E13.MirrorCS");Q24=makeQuery(id+"F13.boolean.opBoolean","SPLIT",EDGE,{"disambiguationData":[TD([makeQuery(id+"F13.opExtrude","SWEPT_FACE",FACE,{"disambiguationData":[OSD([sQuery(id+"F12.wireOp",EDGE,"E41.MirrorCS")])]})])],"derivedFrom":makeQuery(id+"F1.opRevolve","SWEPT_EDGE",EDGE,{"disambiguationData":[OSD([subQ0,subQ1])]})});}
            var Q25;
            {var subQ0=sQuery(id+"F0.wireOp",EDGE,"E11.MirrorCS");var subQ1=sQuery(id+"F0.wireOp",EDGE,"E15.MirrorCS");Q25=makeQuery(id+"F3.boolean.opBoolean","SPLIT",EDGE,{"disambiguationData":[TD([makeQuery(id+"F1.opRevolve","SWEPT_FACE",FACE,{"disambiguationData":[OSD([sQuery(id+"F0.wireOp",EDGE,"E3"),subQ0])]}),makeQuery(id+"F1.opRevolve","SWEPT_FACE",FACE,{"disambiguationData":[OSD([subQ1])]}),makeQuery(id+"F3.opExtrude","SWEPT_FACE",FACE,{"disambiguationData":[OSD([sQuery(id+"F2.wireOp",EDGE,"E18.top")])]}),makeQuery(id+"F3.opExtrude","SWEPT_FACE",FACE,{"disambiguationData":[OSD([sQuery(id+"F2.wireOp",EDGE,"E18.right")])]})])],"derivedFrom":makeQuery(id+"F1.opRevolve","SWEPT_EDGE",EDGE,{"disambiguationData":[OSD([subQ0,subQ1])]})});}
            chamfer(context, id + "F14", {"entities" : qUnion([Q0, Q1, Q2, Q3, Q4, Q5, Q6, Q7, Q8, Q9, Q10, Q11, Q12, Q13, Q14, Q15, Q16, Q17, Q18, Q19, Q20, Q21, Q22, Q23, Q24, Q25]), "width" : 0.5 * mm, "tangentPropagation" : true});
        }
        {
            var Q0;
            Q0=makeQuery(id+"F13.boolean.opBoolean","COPY",EDGE,{"derivedFrom":makeQuery(id+"F13.opExtrude","SWEPT_EDGE",EDGE,{"disambiguationData":[OSD([sQuery(id+"F0.wireOp",EDGE,"E9.MirrorCS"),sQuery(id+"F0.wireOp",EDGE,"E13.MirrorCS"),sQuery(id+"F12.wireOp",EDGE,"E44.3.0"),sQuery(id+"F12.wireOp",EDGE,"E44.3.1")])]})});
            var Q1;
            Q1=makeQuery(id+"F13.boolean.opBoolean","COPY",EDGE,{"derivedFrom":makeQuery(id+"F13.opExtrude","SWEPT_EDGE",EDGE,{"disambiguationData":[OSD([sQuery(id+"F0.wireOp",EDGE,"E9.MirrorCS"),sQuery(id+"F0.wireOp",EDGE,"E13.MirrorCS"),sQuery(id+"F12.wireOp",EDGE,"E44.3.2"),sQuery(id+"F12.wireOp",EDGE,"E44.3.3")])]})});
            var Q2;
            Q2=makeQuery(id+"F13.boolean.opBoolean","COPY",EDGE,{"derivedFrom":makeQuery(id+"F13.opExtrude","SWEPT_EDGE",EDGE,{"disambiguationData":[OSD([sQuery(id+"F0.wireOp",EDGE,"E9.MirrorCS"),sQuery(id+"F0.wireOp",EDGE,"E13.MirrorCS"),sQuery(id+"F12.wireOp",EDGE,"E41.MirrorCS"),sQuery(id+"F12.wireOp",EDGE,"E42.MirrorCS")])]})});
            var Q3;
            Q3=makeQuery(id+"F13.boolean.opBoolean","COPY",EDGE,{"derivedFrom":makeQuery(id+"F13.opExtrude","SWEPT_EDGE",EDGE,{"disambiguationData":[OSD([sQuery(id+"F0.wireOp",EDGE,"E9.MirrorCS"),sQuery(id+"F0.wireOp",EDGE,"E13.MirrorCS"),sQuery(id+"F12.wireOp",EDGE,"E38"),sQuery(id+"F12.wireOp",EDGE,"E39")])]})});
            var Q4;
            Q4=makeQuery(id+"F13.boolean.opBoolean","COPY",EDGE,{"derivedFrom":makeQuery(id+"F13.opExtrude","SWEPT_EDGE",EDGE,{"disambiguationData":[OSD([sQuery(id+"F0.wireOp",EDGE,"E9.MirrorCS"),sQuery(id+"F0.wireOp",EDGE,"E14.MirrorCS"),sQuery(id+"F12.wireOp",EDGE,"E38"),sQuery(id+"F12.wireOp",EDGE,"E40")])]})});
            var Q5;
            Q5=makeQuery(id+"F13.boolean.opBoolean","COPY",EDGE,{"derivedFrom":makeQuery(id+"F13.opExtrude","SWEPT_EDGE",EDGE,{"disambiguationData":[OSD([sQuery(id+"F0.wireOp",EDGE,"E9.MirrorCS"),sQuery(id+"F0.wireOp",EDGE,"E14.MirrorCS"),sQuery(id+"F12.wireOp",EDGE,"E44.3.3"),sQuery(id+"F12.wireOp",EDGE,"E44.3.4")])]})});
            var Q6;
            Q6=makeQuery(id+"F13.boolean.opBoolean","COPY",EDGE,{"derivedFrom":makeQuery(id+"F13.opExtrude","SWEPT_EDGE",EDGE,{"disambiguationData":[OSD([sQuery(id+"F0.wireOp",EDGE,"E9.MirrorCS"),sQuery(id+"F0.wireOp",EDGE,"E14.MirrorCS"),sQuery(id+"F12.wireOp",EDGE,"E44.2.3"),sQuery(id+"F12.wireOp",EDGE,"E44.2.4")])]})});
            var Q7;
            Q7=makeQuery(id+"F13.boolean.opBoolean","COPY",EDGE,{"derivedFrom":makeQuery(id+"F13.opExtrude","SWEPT_EDGE",EDGE,{"disambiguationData":[OSD([sQuery(id+"F0.wireOp",EDGE,"E9.MirrorCS"),sQuery(id+"F0.wireOp",EDGE,"E14.MirrorCS"),sQuery(id+"F12.wireOp",EDGE,"E44.2.0"),sQuery(id+"F12.wireOp",EDGE,"E44.2.5")])]})});
            var Q8;
            Q8=makeQuery(id+"F13.boolean.opBoolean","COPY",EDGE,{"derivedFrom":makeQuery(id+"F13.opExtrude","SWEPT_EDGE",EDGE,{"disambiguationData":[OSD([sQuery(id+"F0.wireOp",EDGE,"E9.MirrorCS"),sQuery(id+"F0.wireOp",EDGE,"E14.MirrorCS"),sQuery(id+"F12.wireOp",EDGE,"E44.1.0"),sQuery(id+"F12.wireOp",EDGE,"E44.1.5")])]})});
            var Q9;
            Q9=makeQuery(id+"F13.boolean.opBoolean","COPY",EDGE,{"derivedFrom":makeQuery(id+"F13.opExtrude","SWEPT_EDGE",EDGE,{"disambiguationData":[OSD([sQuery(id+"F0.wireOp",EDGE,"E9.MirrorCS"),sQuery(id+"F0.wireOp",EDGE,"E14.MirrorCS"),sQuery(id+"F12.wireOp",EDGE,"E44.1.3"),sQuery(id+"F12.wireOp",EDGE,"E44.1.4")])]})});
            var Q10;
            Q10=makeQuery(id+"F13.boolean.opBoolean","COPY",EDGE,{"derivedFrom":makeQuery(id+"F13.opExtrude","SWEPT_EDGE",EDGE,{"disambiguationData":[OSD([sQuery(id+"F0.wireOp",EDGE,"E9.MirrorCS"),sQuery(id+"F0.wireOp",EDGE,"E14.MirrorCS"),sQuery(id+"F12.wireOp",EDGE,"E44.3.0"),sQuery(id+"F12.wireOp",EDGE,"E44.3.5")])]})});
            var Q11;
            Q11=makeQuery(id+"F13.boolean.opBoolean","COPY",EDGE,{"derivedFrom":makeQuery(id+"F13.opExtrude","SWEPT_EDGE",EDGE,{"disambiguationData":[OSD([sQuery(id+"F0.wireOp",EDGE,"E9.MirrorCS"),sQuery(id+"F0.wireOp",EDGE,"E13.MirrorCS"),sQuery(id+"F12.wireOp",EDGE,"E44.2.0"),sQuery(id+"F12.wireOp",EDGE,"E44.2.1")])]})});
            var Q12;
            Q12=makeQuery(id+"F13.boolean.opBoolean","COPY",EDGE,{"derivedFrom":makeQuery(id+"F13.opExtrude","SWEPT_EDGE",EDGE,{"disambiguationData":[OSD([sQuery(id+"F0.wireOp",EDGE,"E9.MirrorCS"),sQuery(id+"F0.wireOp",EDGE,"E13.MirrorCS"),sQuery(id+"F12.wireOp",EDGE,"E44.2.2"),sQuery(id+"F12.wireOp",EDGE,"E44.2.3")])]})});
            var Q13;
            Q13=makeQuery(id+"F13.boolean.opBoolean","COPY",EDGE,{"derivedFrom":makeQuery(id+"F13.opExtrude","SWEPT_EDGE",EDGE,{"disambiguationData":[OSD([sQuery(id+"F0.wireOp",EDGE,"E9.MirrorCS"),sQuery(id+"F0.wireOp",EDGE,"E13.MirrorCS"),sQuery(id+"F12.wireOp",EDGE,"E44.1.2"),sQuery(id+"F12.wireOp",EDGE,"E44.1.3")])]})});
            var Q14;
            Q14=makeQuery(id+"F13.boolean.opBoolean","COPY",EDGE,{"derivedFrom":makeQuery(id+"F13.opExtrude","SWEPT_EDGE",EDGE,{"disambiguationData":[OSD([sQuery(id+"F0.wireOp",EDGE,"E9.MirrorCS"),sQuery(id+"F0.wireOp",EDGE,"E13.MirrorCS"),sQuery(id+"F12.wireOp",EDGE,"E44.1.0"),sQuery(id+"F12.wireOp",EDGE,"E44.1.1")])]})});
            var Q15;
            Q15=makeQuery(id+"F5.boolean.opBoolean","COPY",EDGE,{"derivedFrom":makeQuery(id+"F5.opExtrude","SWEPT_EDGE",EDGE,{"disambiguationData":[OSD([sQuery(id+"F0.wireOp",EDGE,"E1"),sQuery(id+"F0.wireOp",EDGE,"E4"),sQuery(id+"F4.wireOp",EDGE,"E27.3.3"),sQuery(id+"F4.wireOp",EDGE,"E27.3.4")])]})});
            var Q16;
            Q16=makeQuery(id+"F5.boolean.opBoolean","COPY",EDGE,{"derivedFrom":makeQuery(id+"F5.opExtrude","SWEPT_EDGE",EDGE,{"disambiguationData":[OSD([sQuery(id+"F0.wireOp",EDGE,"E1"),sQuery(id+"F0.wireOp",EDGE,"E4"),sQuery(id+"F4.wireOp",EDGE,"E27.2.0"),sQuery(id+"F4.wireOp",EDGE,"E27.2.5")])]})});
            var Q17;
            Q17=makeQuery(id+"F5.boolean.opBoolean","COPY",EDGE,{"derivedFrom":makeQuery(id+"F5.opExtrude","SWEPT_EDGE",EDGE,{"disambiguationData":[OSD([sQuery(id+"F0.wireOp",EDGE,"E1"),sQuery(id+"F0.wireOp",EDGE,"E4"),sQuery(id+"F4.wireOp",EDGE,"E27.2.3"),sQuery(id+"F4.wireOp",EDGE,"E27.2.4")])]})});
            var Q18;
            Q18=makeQuery(id+"F5.boolean.opBoolean","COPY",EDGE,{"derivedFrom":makeQuery(id+"F5.opExtrude","SWEPT_EDGE",EDGE,{"disambiguationData":[OSD([sQuery(id+"F0.wireOp",EDGE,"E1"),sQuery(id+"F0.wireOp",EDGE,"E4"),sQuery(id+"F4.wireOp",EDGE,"E27.1.0"),sQuery(id+"F4.wireOp",EDGE,"E27.1.5")])]})});
            var Q19;
            Q19=makeQuery(id+"F5.boolean.opBoolean","COPY",EDGE,{"derivedFrom":makeQuery(id+"F5.opExtrude","SWEPT_EDGE",EDGE,{"disambiguationData":[OSD([sQuery(id+"F0.wireOp",EDGE,"E1"),sQuery(id+"F0.wireOp",EDGE,"E7"),sQuery(id+"F4.wireOp",EDGE,"E27.1.0"),sQuery(id+"F4.wireOp",EDGE,"E27.1.1")])]})});
            var Q20;
            Q20=makeQuery(id+"F5.boolean.opBoolean","COPY",EDGE,{"derivedFrom":makeQuery(id+"F5.opExtrude","SWEPT_EDGE",EDGE,{"disambiguationData":[OSD([sQuery(id+"F0.wireOp",EDGE,"E1"),sQuery(id+"F0.wireOp",EDGE,"E7"),sQuery(id+"F4.wireOp",EDGE,"E27.1.2"),sQuery(id+"F4.wireOp",EDGE,"E27.1.3")])]})});
            var Q21;
            Q21=makeQuery(id+"F5.boolean.opBoolean","COPY",EDGE,{"derivedFrom":makeQuery(id+"F5.opExtrude","SWEPT_EDGE",EDGE,{"disambiguationData":[OSD([sQuery(id+"F0.wireOp",EDGE,"E1"),sQuery(id+"F0.wireOp",EDGE,"E7"),sQuery(id+"F4.wireOp",EDGE,"E21"),sQuery(id+"F4.wireOp",EDGE,"E22")])]})});
            var Q22;
            Q22=makeQuery(id+"F5.boolean.opBoolean","COPY",EDGE,{"derivedFrom":makeQuery(id+"F5.opExtrude","SWEPT_EDGE",EDGE,{"disambiguationData":[OSD([sQuery(id+"F0.wireOp",EDGE,"E1"),sQuery(id+"F0.wireOp",EDGE,"E7"),sQuery(id+"F4.wireOp",EDGE,"E24.MirrorCS"),sQuery(id+"F4.wireOp",EDGE,"E25.MirrorCS")])]})});
            var Q23;
            Q23=makeQuery(id+"F5.boolean.opBoolean","COPY",EDGE,{"derivedFrom":makeQuery(id+"F5.opExtrude","SWEPT_EDGE",EDGE,{"disambiguationData":[OSD([sQuery(id+"F0.wireOp",EDGE,"E1"),sQuery(id+"F0.wireOp",EDGE,"E4"),sQuery(id+"F4.wireOp",EDGE,"E24.MirrorCS"),sQuery(id+"F4.wireOp",EDGE,"E26.MirrorCS")])]})});
            var Q24;
            Q24=makeQuery(id+"F5.boolean.opBoolean","COPY",EDGE,{"derivedFrom":makeQuery(id+"F5.opExtrude","SWEPT_EDGE",EDGE,{"disambiguationData":[OSD([sQuery(id+"F0.wireOp",EDGE,"E1"),sQuery(id+"F0.wireOp",EDGE,"E7"),sQuery(id+"F4.wireOp",EDGE,"E27.3.2"),sQuery(id+"F4.wireOp",EDGE,"E27.3.3")])]})});
            var Q25;
            Q25=makeQuery(id+"F5.boolean.opBoolean","COPY",EDGE,{"derivedFrom":makeQuery(id+"F5.opExtrude","SWEPT_EDGE",EDGE,{"disambiguationData":[OSD([sQuery(id+"F0.wireOp",EDGE,"E1"),sQuery(id+"F0.wireOp",EDGE,"E7"),sQuery(id+"F4.wireOp",EDGE,"E27.2.0"),sQuery(id+"F4.wireOp",EDGE,"E27.2.1")])]})});
            var Q26;
            Q26=makeQuery(id+"F5.boolean.opBoolean","COPY",EDGE,{"derivedFrom":makeQuery(id+"F5.opExtrude","SWEPT_EDGE",EDGE,{"disambiguationData":[OSD([sQuery(id+"F0.wireOp",EDGE,"E1"),sQuery(id+"F0.wireOp",EDGE,"E4"),sQuery(id+"F4.wireOp",EDGE,"E21"),sQuery(id+"F4.wireOp",EDGE,"E23")])]})});
            var Q27;
            Q27=makeQuery(id+"F5.boolean.opBoolean","COPY",EDGE,{"derivedFrom":makeQuery(id+"F5.opExtrude","SWEPT_EDGE",EDGE,{"disambiguationData":[OSD([sQuery(id+"F0.wireOp",EDGE,"E1"),sQuery(id+"F0.wireOp",EDGE,"E7"),sQuery(id+"F4.wireOp",EDGE,"E27.2.2"),sQuery(id+"F4.wireOp",EDGE,"E27.2.3")])]})});
            var Q28;
            Q28=makeQuery(id+"F5.boolean.opBoolean","COPY",EDGE,{"derivedFrom":makeQuery(id+"F5.opExtrude","SWEPT_EDGE",EDGE,{"disambiguationData":[OSD([sQuery(id+"F0.wireOp",EDGE,"E1"),sQuery(id+"F0.wireOp",EDGE,"E7"),sQuery(id+"F4.wireOp",EDGE,"E27.3.0"),sQuery(id+"F4.wireOp",EDGE,"E27.3.1")])]})});
            chamfer(context, id + "F15", {"entities" : qUnion([Q0, Q1, Q2, Q3, Q4, Q5, Q6, Q7, Q8, Q9, Q10, Q11, Q12, Q13, Q14, Q15, Q16, Q17, Q18, Q19, Q20, Q21, Q22, Q23, Q24, Q25, Q26, Q27, Q28]), "width" : 0.2 * mm, "tangentPropagation" : true});
        }
        {
            var Q0;
            Q0=makeQuery(id+"F1.opRevolve","SWEPT_EDGE",EDGE,{"disambiguationData":[OSD([sQuery(id+"F0.wireOp",EDGE,"E4"),sQuery(id+"F0.wireOp",EDGE,"E5")])]});
            var Q1;
            {var subQ0=sQuery(id+"F0.wireOp",EDGE,"E2");var subQ1=sQuery(id+"F0.wireOp",EDGE,"E7");Q1=makeQuery(id+"F3.boolean.opBoolean","SPLIT",EDGE,{"disambiguationData":[TD([makeQuery(id+"F1.opRevolve","SWEPT_FACE",FACE,{"disambiguationData":[OSD([subQ0])]}),makeQuery(id+"F1.opRevolve","SWEPT_FACE",FACE,{"disambiguationData":[OSD([subQ1])]}),makeQuery(id+"F3.opExtrude","SWEPT_FACE",FACE,{"disambiguationData":[OSD([sQuery(id+"F2.wireOp",EDGE,"E18.top")])]}),makeQuery(id+"F3.opExtrude","SWEPT_FACE",FACE,{"disambiguationData":[OSD([sQuery(id+"F2.wireOp",EDGE,"E18.left")])]})])],"derivedFrom":makeQuery(id+"F1.opRevolve","SWEPT_EDGE",EDGE,{"disambiguationData":[OSD([subQ0,subQ1])]})});}
            var Q2;
            Q2=makeQuery(id+"F1.opRevolve","SWEPT_FACE",FACE,{"disambiguationData":[OSD([sQuery(id+"F0.wireOp",EDGE,"E13.MirrorCS")])]});
            var Q3;
            Q3=makeQuery(id+"F1.opRevolve","SWEPT_EDGE",EDGE,{"disambiguationData":[OSD([sQuery(id+"F0.wireOp",EDGE,"E10.MirrorCS"),sQuery(id+"F0.wireOp",EDGE,"E14.MirrorCS")])]});
            fillet(context, id + "F16", {"entities" : qUnion([Q0, Q1, Q2, Q3]), "radius" : 0.5 * mm, "tangentPropagation" : true, "allowEdgeOverflow" : false});
        }
    });
